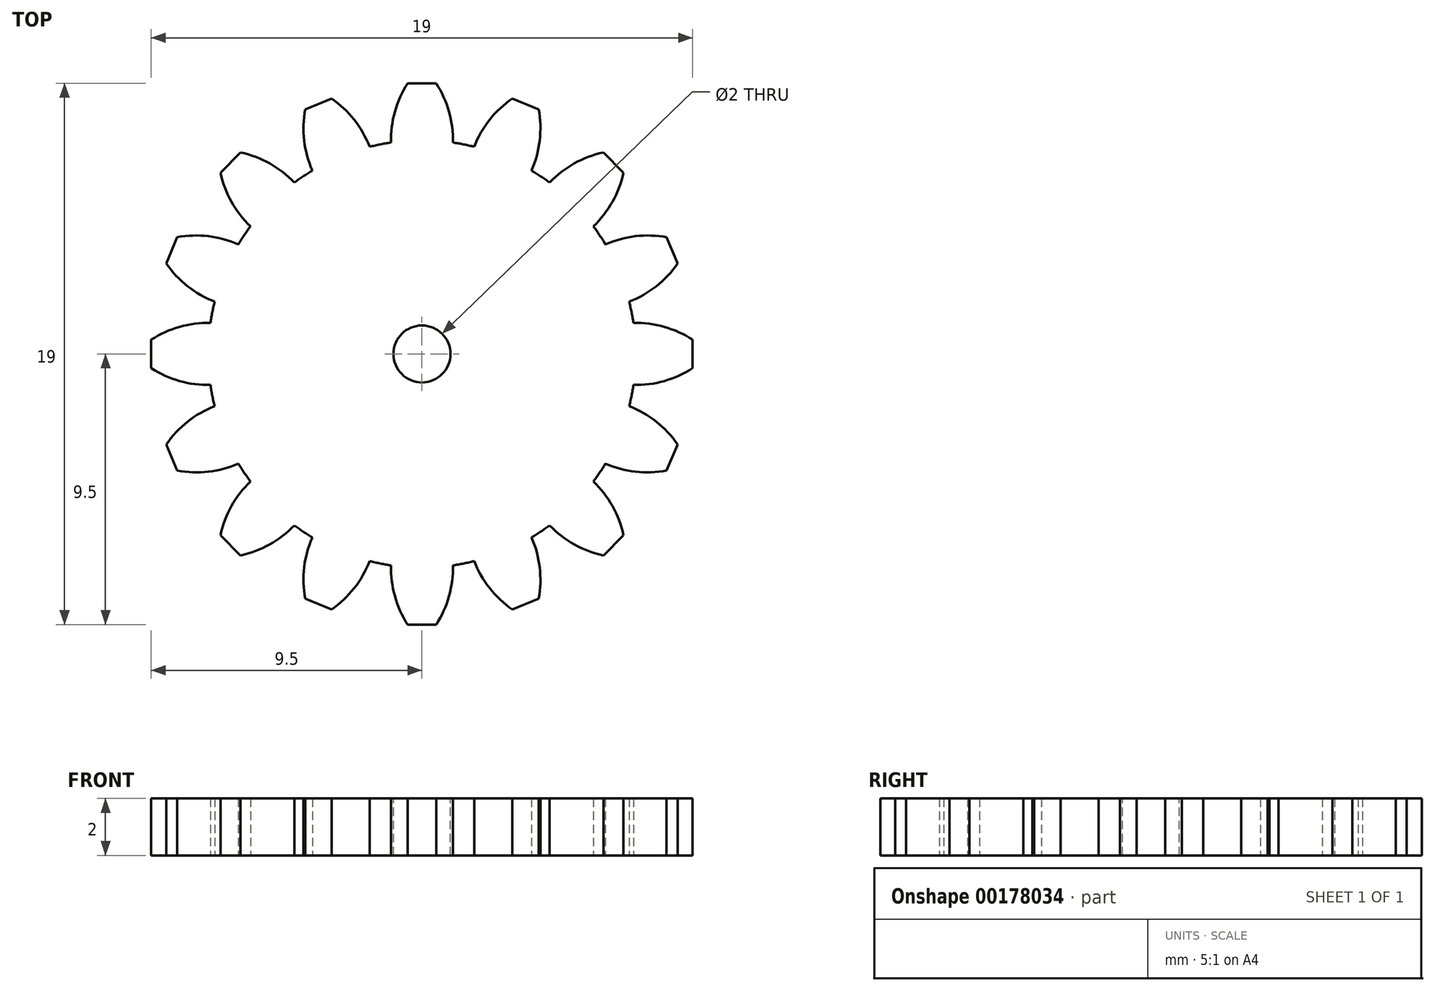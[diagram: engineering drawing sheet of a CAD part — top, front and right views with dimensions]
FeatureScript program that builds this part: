
annotation { "Feature Type Name" : "Feature", "Feature Type Description" : "" }
export const myFeature = defineFeature(function(context is Context, id is Id, definition is map)
    precondition{}
    {
        {
            var Q0;
            Q0=qCreatedBy(makeId("Top.planeOp"),FACE);
            var sketch = newSketch(context, id + "F0", { "sketchPlane" : qUnion([Q0])});
            skCircle(sketch, "E0", {"center": v(0, 0) * mm, "radius": 7.5 * mm});
            skLineSegment(sketch, "E1", {"start": v(0, 0) * mm, "end": v(0, 7.5) * mm, "construction": true});
            skLineSegment(sketch, "E2", {"start": v(0, 9.5) * mm, "end": v(-0.5, 9.5) * mm});
            skArc(sketch, "E3", {"start": v(-0.5, 9.5) * mm, "mid": v(-0.95, 8.5) * mm, "end": v(-1.09, 7.42) * mm});
            skLineSegment(sketch, "E4.MirrorCS", {"start": v(0, 9.5) * mm, "end": v(0.5, 9.5) * mm});
            skArc(sketch, "E5.MirrorCS", {"start": v(0.5, 9.5) * mm, "mid": v(0.95, 8.5) * mm, "end": v(1.09, 7.42) * mm});
            skArc(sketch, "E6.1.0", {"start": v(-4.1, 8.59) * mm, "mid": v(-4.13, 7.5) * mm, "end": v(-3.85, 6.44) * mm});
            skLineSegment(sketch, "E6.1.1", {"start": v(-3.64, 8.78) * mm, "end": v(-4.1, 8.59) * mm});
            skLineSegment(sketch, "E6.1.2", {"start": v(-3.64, 8.78) * mm, "end": v(-3.17, 8.97) * mm});
            skArc(sketch, "E6.1.3", {"start": v(-3.17, 8.97) * mm, "mid": v(-2.38, 8.22) * mm, "end": v(-1.83, 7.27) * mm});
            skArc(sketch, "E6.2.0", {"start": v(-7.07, 6.36) * mm, "mid": v(-6.69, 5.34) * mm, "end": v(-6.02, 4.48) * mm});
            skLineSegment(sketch, "E6.2.1", {"start": v(-6.72, 6.72) * mm, "end": v(-7.07, 6.36) * mm});
            skLineSegment(sketch, "E6.2.2", {"start": v(-6.72, 6.72) * mm, "end": v(-6.36, 7.07) * mm});
            skArc(sketch, "E6.2.3", {"start": v(-6.36, 7.07) * mm, "mid": v(-5.34, 6.69) * mm, "end": v(-4.48, 6.02) * mm});
            skArc(sketch, "E6.3.0", {"start": v(-8.97, 3.17) * mm, "mid": v(-8.22, 2.38) * mm, "end": v(-7.27, 1.83) * mm});
            skLineSegment(sketch, "E6.3.1", {"start": v(-8.78, 3.64) * mm, "end": v(-8.97, 3.17) * mm});
            skLineSegment(sketch, "E6.3.2", {"start": v(-8.78, 3.64) * mm, "end": v(-8.59, 4.1) * mm});
            skArc(sketch, "E6.3.3", {"start": v(-8.59, 4.1) * mm, "mid": v(-7.5, 4.13) * mm, "end": v(-6.44, 3.85) * mm});
            skArc(sketch, "E6.4.0", {"start": v(-9.5, -0.5) * mm, "mid": v(-8.5, -0.95) * mm, "end": v(-7.42, -1.09) * mm});
            skLineSegment(sketch, "E6.4.1", {"start": v(-9.5, 0) * mm, "end": v(-9.5, -0.5) * mm});
            skLineSegment(sketch, "E6.4.2", {"start": v(-9.5, 0) * mm, "end": v(-9.5, 0.5) * mm});
            skArc(sketch, "E6.4.3", {"start": v(-9.5, 0.5) * mm, "mid": v(-8.5, 0.95) * mm, "end": v(-7.42, 1.09) * mm});
            skArc(sketch, "E6.5.0", {"start": v(-8.59, -4.1) * mm, "mid": v(-7.5, -4.13) * mm, "end": v(-6.44, -3.85) * mm});
            skLineSegment(sketch, "E6.5.1", {"start": v(-8.78, -3.64) * mm, "end": v(-8.59, -4.1) * mm});
            skLineSegment(sketch, "E6.5.2", {"start": v(-8.78, -3.64) * mm, "end": v(-8.97, -3.17) * mm});
            skArc(sketch, "E6.5.3", {"start": v(-8.97, -3.17) * mm, "mid": v(-8.22, -2.38) * mm, "end": v(-7.27, -1.83) * mm});
            skArc(sketch, "E6.6.0", {"start": v(-6.36, -7.07) * mm, "mid": v(-5.34, -6.69) * mm, "end": v(-4.48, -6.02) * mm});
            skLineSegment(sketch, "E6.6.1", {"start": v(-6.72, -6.72) * mm, "end": v(-6.36, -7.07) * mm});
            skLineSegment(sketch, "E6.6.2", {"start": v(-6.72, -6.72) * mm, "end": v(-7.07, -6.36) * mm});
            skArc(sketch, "E6.6.3", {"start": v(-7.07, -6.36) * mm, "mid": v(-6.69, -5.34) * mm, "end": v(-6.02, -4.48) * mm});
            skArc(sketch, "E6.7.0", {"start": v(-3.17, -8.97) * mm, "mid": v(-2.38, -8.22) * mm, "end": v(-1.83, -7.27) * mm});
            skLineSegment(sketch, "E6.7.1", {"start": v(-3.64, -8.78) * mm, "end": v(-3.17, -8.97) * mm});
            skLineSegment(sketch, "E6.7.2", {"start": v(-3.64, -8.78) * mm, "end": v(-4.1, -8.59) * mm});
            skArc(sketch, "E6.7.3", {"start": v(-4.1, -8.59) * mm, "mid": v(-4.13, -7.5) * mm, "end": v(-3.85, -6.44) * mm});
            skArc(sketch, "E6.8.0", {"start": v(0.5, -9.5) * mm, "mid": v(0.95, -8.5) * mm, "end": v(1.09, -7.42) * mm});
            skLineSegment(sketch, "E6.8.1", {"start": v(0, -9.5) * mm, "end": v(0.5, -9.5) * mm});
            skLineSegment(sketch, "E6.8.2", {"start": v(0, -9.5) * mm, "end": v(-0.5, -9.5) * mm});
            skArc(sketch, "E6.8.3", {"start": v(-0.5, -9.5) * mm, "mid": v(-0.95, -8.5) * mm, "end": v(-1.09, -7.42) * mm});
            skArc(sketch, "E6.9.0", {"start": v(4.1, -8.59) * mm, "mid": v(4.13, -7.5) * mm, "end": v(3.85, -6.44) * mm});
            skLineSegment(sketch, "E6.9.1", {"start": v(3.64, -8.78) * mm, "end": v(4.1, -8.59) * mm});
            skLineSegment(sketch, "E6.9.2", {"start": v(3.64, -8.78) * mm, "end": v(3.17, -8.97) * mm});
            skArc(sketch, "E6.9.3", {"start": v(3.17, -8.97) * mm, "mid": v(2.38, -8.22) * mm, "end": v(1.83, -7.27) * mm});
            skArc(sketch, "E6.10.0", {"start": v(7.07, -6.36) * mm, "mid": v(6.69, -5.34) * mm, "end": v(6.02, -4.48) * mm});
            skLineSegment(sketch, "E6.10.1", {"start": v(6.72, -6.72) * mm, "end": v(7.07, -6.36) * mm});
            skLineSegment(sketch, "E6.10.2", {"start": v(6.72, -6.72) * mm, "end": v(6.36, -7.07) * mm});
            skArc(sketch, "E6.10.3", {"start": v(6.36, -7.07) * mm, "mid": v(5.34, -6.69) * mm, "end": v(4.48, -6.02) * mm});
            skArc(sketch, "E6.11.0", {"start": v(8.97, -3.17) * mm, "mid": v(8.22, -2.38) * mm, "end": v(7.27, -1.83) * mm});
            skLineSegment(sketch, "E6.11.1", {"start": v(8.78, -3.64) * mm, "end": v(8.97, -3.17) * mm});
            skLineSegment(sketch, "E6.11.2", {"start": v(8.78, -3.64) * mm, "end": v(8.59, -4.1) * mm});
            skArc(sketch, "E6.11.3", {"start": v(8.59, -4.1) * mm, "mid": v(7.5, -4.13) * mm, "end": v(6.44, -3.85) * mm});
            skArc(sketch, "E6.12.0", {"start": v(9.5, 0.5) * mm, "mid": v(8.5, 0.95) * mm, "end": v(7.42, 1.09) * mm});
            skLineSegment(sketch, "E6.12.1", {"start": v(9.5, 0) * mm, "end": v(9.5, 0.5) * mm});
            skLineSegment(sketch, "E6.12.2", {"start": v(9.5, 0) * mm, "end": v(9.5, -0.5) * mm});
            skArc(sketch, "E6.12.3", {"start": v(9.5, -0.5) * mm, "mid": v(8.5, -0.95) * mm, "end": v(7.42, -1.09) * mm});
            skArc(sketch, "E6.13.0", {"start": v(8.59, 4.1) * mm, "mid": v(7.5, 4.13) * mm, "end": v(6.44, 3.85) * mm});
            skLineSegment(sketch, "E6.13.1", {"start": v(8.78, 3.64) * mm, "end": v(8.59, 4.1) * mm});
            skLineSegment(sketch, "E6.13.2", {"start": v(8.78, 3.64) * mm, "end": v(8.97, 3.17) * mm});
            skArc(sketch, "E6.13.3", {"start": v(8.97, 3.17) * mm, "mid": v(8.22, 2.38) * mm, "end": v(7.27, 1.83) * mm});
            skArc(sketch, "E6.14.0", {"start": v(6.36, 7.07) * mm, "mid": v(5.34, 6.69) * mm, "end": v(4.48, 6.02) * mm});
            skLineSegment(sketch, "E6.14.1", {"start": v(6.72, 6.72) * mm, "end": v(6.36, 7.07) * mm});
            skLineSegment(sketch, "E6.14.2", {"start": v(6.72, 6.72) * mm, "end": v(7.07, 6.36) * mm});
            skArc(sketch, "E6.14.3", {"start": v(7.07, 6.36) * mm, "mid": v(6.69, 5.34) * mm, "end": v(6.02, 4.48) * mm});
            skArc(sketch, "E6.15.0", {"start": v(3.17, 8.97) * mm, "mid": v(2.38, 8.22) * mm, "end": v(1.83, 7.27) * mm});
            skLineSegment(sketch, "E6.15.1", {"start": v(3.64, 8.78) * mm, "end": v(3.17, 8.97) * mm});
            skLineSegment(sketch, "E6.15.2", {"start": v(3.64, 8.78) * mm, "end": v(4.1, 8.59) * mm});
            skArc(sketch, "E6.15.3", {"start": v(4.1, 8.59) * mm, "mid": v(4.13, 7.5) * mm, "end": v(3.85, 6.44) * mm});
            skSolve(sketch);
        }
        {
            var Q0;
            Q0=qSketchRegion(id+"F0",true);
            extrude(context, id + "F1", {"entities" : qUnion([Q0]), "depth" : 2 * mm});
        }
        {
            var Q0;
            Q0=makeQuery(id+"F1.opExtrude","CAP_FACE",FACE,{"disambiguationData":[OSD([sQuery(id+"F0.wireOp",EDGE,"E0"),sQuery(id+"F0.wireOp",EDGE,"E2"),sQuery(id+"F0.wireOp",EDGE,"E3"),sQuery(id+"F0.wireOp",EDGE,"E4.MirrorCS"),sQuery(id+"F0.wireOp",EDGE,"E5.MirrorCS"),sQuery(id+"F0.wireOp",EDGE,"E6.1.0"),sQuery(id+"F0.wireOp",EDGE,"E6.1.1"),sQuery(id+"F0.wireOp",EDGE,"E6.1.2"),sQuery(id+"F0.wireOp",EDGE,"E6.1.3"),sQuery(id+"F0.wireOp",EDGE,"E6.2.0"),sQuery(id+"F0.wireOp",EDGE,"E6.2.1"),sQuery(id+"F0.wireOp",EDGE,"E6.2.2"),sQuery(id+"F0.wireOp",EDGE,"E6.2.3"),sQuery(id+"F0.wireOp",EDGE,"E6.3.0"),sQuery(id+"F0.wireOp",EDGE,"E6.3.1"),sQuery(id+"F0.wireOp",EDGE,"E6.3.2"),sQuery(id+"F0.wireOp",EDGE,"E6.3.3"),sQuery(id+"F0.wireOp",EDGE,"E6.4.0"),sQuery(id+"F0.wireOp",EDGE,"E6.4.1"),sQuery(id+"F0.wireOp",EDGE,"E6.4.2"),sQuery(id+"F0.wireOp",EDGE,"E6.4.3"),sQuery(id+"F0.wireOp",EDGE,"E6.5.0"),sQuery(id+"F0.wireOp",EDGE,"E6.5.1"),sQuery(id+"F0.wireOp",EDGE,"E6.5.2"),sQuery(id+"F0.wireOp",EDGE,"E6.5.3"),sQuery(id+"F0.wireOp",EDGE,"E6.6.0"),sQuery(id+"F0.wireOp",EDGE,"E6.6.1"),sQuery(id+"F0.wireOp",EDGE,"E6.6.2"),sQuery(id+"F0.wireOp",EDGE,"E6.6.3"),sQuery(id+"F0.wireOp",EDGE,"E6.7.0"),sQuery(id+"F0.wireOp",EDGE,"E6.7.1"),sQuery(id+"F0.wireOp",EDGE,"E6.7.2"),sQuery(id+"F0.wireOp",EDGE,"E6.7.3"),sQuery(id+"F0.wireOp",EDGE,"E6.8.0"),sQuery(id+"F0.wireOp",EDGE,"E6.8.1"),sQuery(id+"F0.wireOp",EDGE,"E6.8.2"),sQuery(id+"F0.wireOp",EDGE,"E6.8.3"),sQuery(id+"F0.wireOp",EDGE,"E6.9.0"),sQuery(id+"F0.wireOp",EDGE,"E6.9.1"),sQuery(id+"F0.wireOp",EDGE,"E6.9.2"),sQuery(id+"F0.wireOp",EDGE,"E6.9.3"),sQuery(id+"F0.wireOp",EDGE,"E6.10.0"),sQuery(id+"F0.wireOp",EDGE,"E6.10.1"),sQuery(id+"F0.wireOp",EDGE,"E6.10.2"),sQuery(id+"F0.wireOp",EDGE,"E6.10.3"),sQuery(id+"F0.wireOp",EDGE,"E6.11.0"),sQuery(id+"F0.wireOp",EDGE,"E6.11.1"),sQuery(id+"F0.wireOp",EDGE,"E6.11.2"),sQuery(id+"F0.wireOp",EDGE,"E6.11.3"),sQuery(id+"F0.wireOp",EDGE,"E6.12.0"),sQuery(id+"F0.wireOp",EDGE,"E6.12.1"),sQuery(id+"F0.wireOp",EDGE,"E6.12.2"),sQuery(id+"F0.wireOp",EDGE,"E6.12.3"),sQuery(id+"F0.wireOp",EDGE,"E6.13.0"),sQuery(id+"F0.wireOp",EDGE,"E6.13.1"),sQuery(id+"F0.wireOp",EDGE,"E6.13.2"),sQuery(id+"F0.wireOp",EDGE,"E6.13.3"),sQuery(id+"F0.wireOp",EDGE,"E6.14.0"),sQuery(id+"F0.wireOp",EDGE,"E6.14.1"),sQuery(id+"F0.wireOp",EDGE,"E6.14.2"),sQuery(id+"F0.wireOp",EDGE,"E6.14.3"),sQuery(id+"F0.wireOp",EDGE,"E6.15.0"),sQuery(id+"F0.wireOp",EDGE,"E6.15.1"),sQuery(id+"F0.wireOp",EDGE,"E6.15.2"),sQuery(id+"F0.wireOp",EDGE,"E6.15.3")])],"isStart":false});
            var sketch = newSketch(context, id + "F2", { "sketchPlane" : qUnion([Q0])});
            skCircle(sketch, "E7", {"center": v(0, 0) * mm, "radius": 1 * mm});
            skSolve(sketch);
        }
        {
            var Q0;
            Q0=qSketchRegion(id+"F2",true);
            extrude(context, id + "F3", {"entities" : qUnion([Q0]), "operationType" : NewBodyOperationType.REMOVE, "endBound" : BoundingType.THROUGH_ALL, "oppositeDirection" : true, "depth" : 25 * mm});
        }
    });
